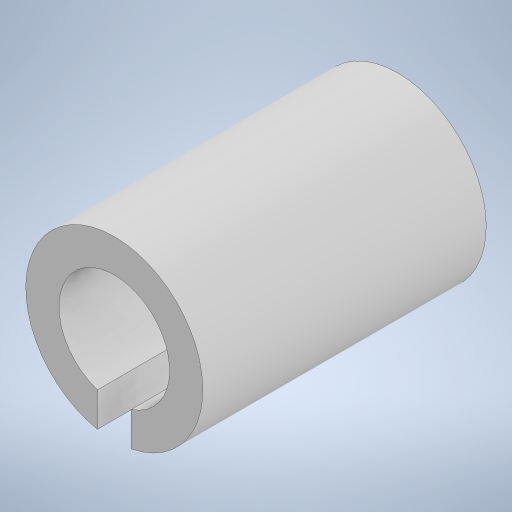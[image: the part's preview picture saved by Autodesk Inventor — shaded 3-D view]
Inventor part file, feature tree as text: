
AUTODESK INVENTOR PART (.ipt)
format: ipt  version: 2023 (Build 270158000, 158)  size: 206,336 bytes
history: native  units: in
note: dims shown in document units (in); Inventor stores cm internally (conversion verified against a paired STEP export)
features: extrude x1, sketch x1
ambient origin geometry x8: Origin, YZ Plane, XZ Plane, XY Plane, X Axis, Y Axis, Z Axis, Center Point
bodies: Solid1 (feature_tree)
feature tree (2):
  extrude  "Extrusion1"  Depth=0.2in
  sketch  "Sketch1"  dims[d0=0.125in d1=0.0781in d2=0.2in d3=0.0in]
